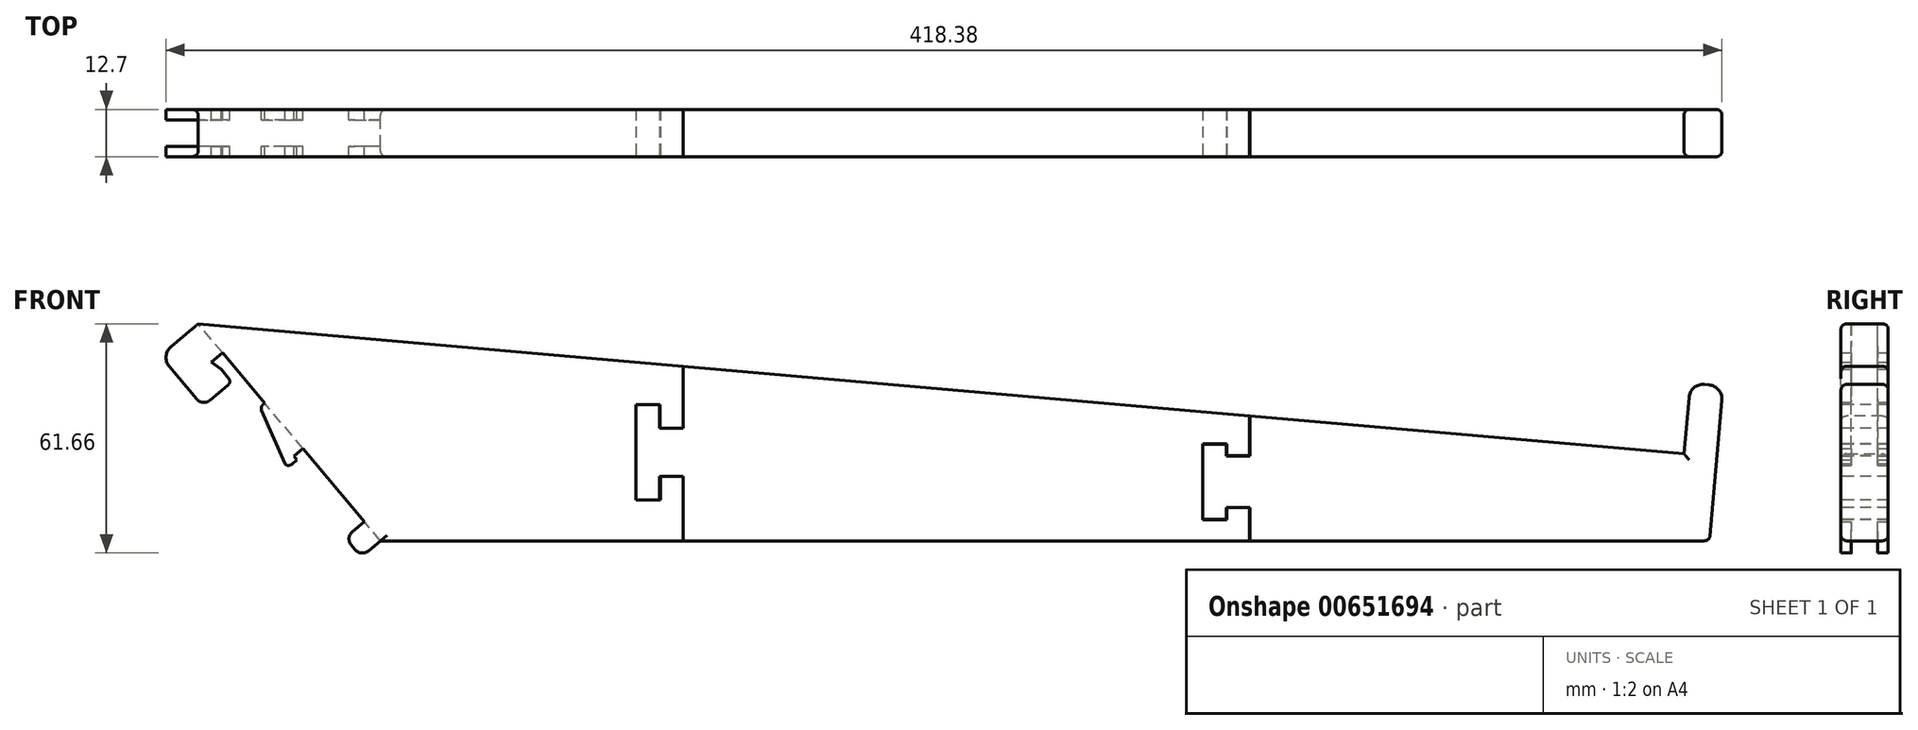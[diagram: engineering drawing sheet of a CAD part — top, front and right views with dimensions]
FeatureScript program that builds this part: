
annotation { "Feature Type Name" : "Feature", "Feature Type Description" : "" }
export const myFeature = defineFeature(function(context is Context, id is Id, definition is map)
    precondition{}
    {
        {
            var Q0;
            Q0=qCreatedBy(makeId("Front.planeOp"),FACE);
            var sketch = newSketch(context, id + "F0", { "sketchPlane" : qUnion([Q0])});
            skLineSegment(sketch, "E0.left", {"start": v(-46.53, -20.75) * mm, "end": v(-39.18, -29.5) * mm});
            skLineSegment(sketch, "E1", {"start": v(-38.77, -9.26) * mm, "end": v(360.76, -44.2) * mm});
            skLineSegment(sketch, "E2", {"start": v(360.76, -44.2) * mm, "end": v(362.09, -29.03) * mm});
            skLineSegment(sketch, "E3", {"start": v(10.22, -67.63) * mm, "end": v(367.63, -67.63) * mm});
            skPoint(sketch, "E4.start.orphan", {"position": v(-14.28, -38.44) * mm});
            skLineSegment(sketch, "E5.0", {"start": v(367.63, -67.63) * mm, "end": v(370.94, -29.8) * mm});
            skLineSegment(sketch, "E6.0", {"start": v(366.22, -25.56) * mm, "end": v(367.48, -25.67) * mm});
            skLineSegment(sketch, "E7", {"start": v(-46.06, -15.38) * mm, "end": v(-38.77, -9.26) * mm});
            skLineSegment(sketch, "E8", {"start": v(7, -70.32) * mm, "end": v(10.22, -67.63) * mm});
            skLineSegment(sketch, "E9.0", {"start": v(-12.22, -45.83) * mm, "end": v(-13.03, -44.86) * mm});
            skLineSegment(sketch, "E10.0", {"start": v(-35.6, -29.82) * mm, "end": v(-30.74, -25.73) * mm});
            skLineSegment(sketch, "E11.0", {"start": v(-30.58, -23.94) * mm, "end": v(-32.63, -21.51) * mm});
            skLineSegment(sketch, "E12.0", {"start": v(5.89, -62.47) * mm, "end": v(-10.6, -42.82) * mm});
            skLineSegment(sketch, "E13", {"start": v(-39.18, -29.5) * mm, "end": v(-46.53, -20.75) * mm});
            skLineSegment(sketch, "E14", {"start": v(-35.22, -19.55) * mm, "end": v(-32.23, -17.04) * mm});
            skArc(sketch, "E15.filletArc", {"start": v(-39.18, -29.5) * mm, "mid": v(-37.46, -30.4) * mm, "end": v(-35.6, -29.82) * mm});
            skArc(sketch, "E16.filletArc", {"start": v(-30.74, -25.73) * mm, "mid": v(-30.3, -24.87) * mm, "end": v(-30.58, -23.94) * mm});
            skLineSegment(sketch, "E17.0", {"start": v(-13.03, -44.86) * mm, "end": v(-10.6, -42.82) * mm});
            skLineSegment(sketch, "E18.0", {"start": v(6.99, -43.82) * mm, "end": v(6.99, -43.82) * mm});
            skLineSegment(sketch, "E19.0", {"start": v(-13.68, -47.06) * mm, "end": v(-12.22, -45.83) * mm});
            skLineSegment(sketch, "E20.0", {"start": v(-21.37, -30.97) * mm, "end": v(-20.89, -30.56) * mm});
            skLineSegment(sketch, "E21", {"start": v(-21.72, -32.45) * mm, "end": v(-15.47, -46.9) * mm});
            skLineSegment(sketch, "E22.trimOffspring", {"start": v(-20.89, -30.56) * mm, "end": v(-32.23, -17.04) * mm});
            skLineSegment(sketch, "E23.0", {"start": v(2.68, -65.17) * mm, "end": v(5.89, -62.47) * mm});
            skLineSegment(sketch, "E24.0", {"start": v(3.43, -70) * mm, "end": v(2.37, -68.74) * mm});
            skArc(sketch, "E25.filletArc", {"start": v(2.68, -65.17) * mm, "mid": v(1.78, -66.9) * mm, "end": v(2.37, -68.74) * mm});
            skArc(sketch, "E26.filletArc", {"start": v(3.43, -70) * mm, "mid": v(5.15, -70.9) * mm, "end": v(7, -70.32) * mm});
            skPoint(sketch, "E27.visualSharp", {"position": v(-14.65, -47.87) * mm});
            skArc(sketch, "E27.filletArc", {"start": v(-15.47, -46.9) * mm, "mid": v(-14.6, -47.35) * mm, "end": v(-13.68, -47.06) * mm});
            skPoint(sketch, "E28.visualSharp", {"position": v(-22.1, -31.58) * mm});
            skArc(sketch, "E28.filletArc", {"start": v(-21.37, -30.97) * mm, "mid": v(-21.8, -31.65) * mm, "end": v(-21.72, -32.45) * mm});
            skPoint(sketch, "E29.visualSharp", {"position": v(371.28, -26) * mm});
            skArc(sketch, "E29.filletArc", {"start": v(370.94, -29.8) * mm, "mid": v(370.07, -27.02) * mm, "end": v(367.48, -25.67) * mm});
            skPoint(sketch, "E30.visualSharp", {"position": v(362.42, -25.23) * mm});
            skArc(sketch, "E30.filletArc", {"start": v(366.22, -25.56) * mm, "mid": v(363.43, -26.44) * mm, "end": v(362.09, -29.03) * mm});
            skPoint(sketch, "E31.visualSharp", {"position": v(-48.98, -17.83) * mm});
            skArc(sketch, "E31.filletArc", {"start": v(-46.06, -15.38) * mm, "mid": v(-47.4, -17.96) * mm, "end": v(-46.53, -20.75) * mm});
            skLineSegment(sketch, "E32", {"start": v(-32.63, -21.51) * mm, "end": v(-35.22, -19.55) * mm});
            skPoint(sketch, "E33.orphan", {"position": v(-34.67, -19.08) * mm});
            skPoint(sketch, "E34.filletArc.end.orphan", {"position": v(367.94, -64.15) * mm});
            skSolve(sketch);
        }
        {
            var Q0;
            Q0=qSketchRegion(id+"F0",true);
            extrude(context, id + "F1", {"entities" : qUnion([Q0]), "depth" : 12.7 * mm, "offsetDistance" : 25.4 * mm});
        }
        {
            var Q0;
            Q0=makeQuery(id+"F1.opExtrude","SWEPT_FACE",FACE,{"disambiguationData":[OSD([sQuery(id+"F0.wireOp",EDGE,"E7")])]});
            var sketch = newSketch(context, id + "F2", { "sketchPlane" : qUnion([Q0])});
            skLineSegment(sketch, "E35.0", {"start": v(-48.98, -2.82) * mm, "end": v(-35.65, -2.82) * mm});
            skLineSegment(sketch, "E36.0", {"start": v(-35.65, -9.9) * mm, "end": v(-48.98, -9.9) * mm});
            skLineSegment(sketch, "E37", {"start": v(-35.65, -2.82) * mm, "end": v(-35.65, -9.9) * mm});
            skLineSegment(sketch, "E38", {"start": v(-48.98, -9.9) * mm, "end": v(-48.98, -2.82) * mm});
            skSolve(sketch);
        }
        {
            var Q0;
            Q0=qSketchRegion(id+"F2",true);
            extrude(context, id + "F3", {"entities" : qUnion([Q0]), "operationType" : NewBodyOperationType.REMOVE, "oppositeDirection" : true, "depth" : 93.47 * mm, "offsetDistance" : 25.4 * mm});
        }
        {
            var Q0;
            Q0=makeQuery(id+"F1.opExtrude","CAP_FACE",FACE,{"disambiguationData":[OSD([sQuery(id+"F0.wireOp",EDGE,"E1"),sQuery(id+"F0.wireOp",EDGE,"E2"),sQuery(id+"F0.wireOp",EDGE,"E3"),sQuery(id+"F0.wireOp",EDGE,"E5.0"),sQuery(id+"F0.wireOp",EDGE,"E6.0"),sQuery(id+"F0.wireOp",EDGE,"E7"),sQuery(id+"F0.wireOp",EDGE,"E8"),sQuery(id+"F0.wireOp",EDGE,"E9.0"),sQuery(id+"F0.wireOp",EDGE,"E10.0"),sQuery(id+"F0.wireOp",EDGE,"E12.0"),sQuery(id+"F0.wireOp",EDGE,"E13"),sQuery(id+"F0.wireOp",EDGE,"E14"),sQuery(id+"F0.wireOp",EDGE,"E15.filletArc"),sQuery(id+"F0.wireOp",EDGE,"E16.filletArc"),sQuery(id+"F0.wireOp",EDGE,"E17.0"),sQuery(id+"F0.wireOp",EDGE,"E19.0"),sQuery(id+"F0.wireOp",EDGE,"E20.0"),sQuery(id+"F0.wireOp",EDGE,"E11.0"),sQuery(id+"F0.wireOp",EDGE,"E21"),sQuery(id+"F0.wireOp",EDGE,"E22.trimOffspring"),sQuery(id+"F0.wireOp",EDGE,"E23.0"),sQuery(id+"F0.wireOp",EDGE,"E24.0"),sQuery(id+"F0.wireOp",EDGE,"E25.filletArc"),sQuery(id+"F0.wireOp",EDGE,"E26.filletArc"),sQuery(id+"F0.wireOp",EDGE,"E27.filletArc"),sQuery(id+"F0.wireOp",EDGE,"E28.filletArc"),sQuery(id+"F0.wireOp",EDGE,"E34.filletArc"),sQuery(id+"F0.wireOp",EDGE,"E29.filletArc"),sQuery(id+"F0.wireOp",EDGE,"E30.filletArc")])],"isStart":false});
            var sketch = newSketch(context, id + "F4", { "sketchPlane" : qUnion([Q0])});
            skLineSegment(sketch, "E39.0", {"start": v(91.68, -88.8) * mm, "end": v(91.68, -50.24) * mm});
            skLineSegment(sketch, "E40.0", {"start": v(85.33, -56.6) * mm, "end": v(85.33, -50.24) * mm});
            skLineSegment(sketch, "E41.0", {"start": v(85.33, -50.24) * mm, "end": v(91.68, -50.24) * mm});
            skLineSegment(sketch, "E42.0", {"start": v(85.33, -37.39) * mm, "end": v(91.68, -37.39) * mm});
            skLineSegment(sketch, "E43.0", {"start": v(78.98, -56.6) * mm, "end": v(78.98, -31.04) * mm});
            skLineSegment(sketch, "E44.0", {"start": v(78.98, -56.6) * mm, "end": v(85.33, -56.6) * mm});
            skLineSegment(sketch, "E45.0", {"start": v(78.98, -31.04) * mm, "end": v(85.33, -31.04) * mm});
            skLineSegment(sketch, "E46.trimOffspring", {"start": v(85.33, -37.39) * mm, "end": v(85.33, -31.04) * mm});
            skLineSegment(sketch, "E47.trimOffspring", {"start": v(91.68, -37.39) * mm, "end": v(91.68, 1.17) * mm});
            skLineSegment(sketch, "E48.0", {"start": v(91.58, -88.8) * mm, "end": v(91.58, -50.34) * mm});
            skLineSegment(sketch, "E49.0", {"start": v(85.51, -50.34) * mm, "end": v(91.58, -50.34) * mm});
            skLineSegment(sketch, "E50.0", {"start": v(85.51, -56.7) * mm, "end": v(85.51, -50.34) * mm});
            skLineSegment(sketch, "E51.0", {"start": v(78.88, -56.7) * mm, "end": v(85.51, -56.7) * mm});
            skLineSegment(sketch, "E52.0", {"start": v(78.88, -56.7) * mm, "end": v(78.88, -30.94) * mm});
            skLineSegment(sketch, "E53.0", {"start": v(78.88, -30.94) * mm, "end": v(85.43, -30.94) * mm});
            skLineSegment(sketch, "E54.0", {"start": v(85.43, -37.29) * mm, "end": v(85.43, -30.94) * mm});
            skLineSegment(sketch, "E55.0", {"start": v(85.43, -37.29) * mm, "end": v(91.58, -37.29) * mm});
            skLineSegment(sketch, "E56.0", {"start": v(91.58, -37.29) * mm, "end": v(91.58, 1.17) * mm});
            skLineSegment(sketch, "E57", {"start": v(91.68, -88.8) * mm, "end": v(91.58, -88.8) * mm});
            skLineSegment(sketch, "E58", {"start": v(91.68, 1.17) * mm, "end": v(91.58, 1.17) * mm});
            skLineSegment(sketch, "E59", {"start": v(244, -9.76) * mm, "end": v(244, -44.83) * mm});
            skLineSegment(sketch, "E60", {"start": v(237.73, -41.63) * mm, "end": v(237.73, -44.83) * mm});
            skLineSegment(sketch, "E61.0", {"start": v(231.38, -41.63) * mm, "end": v(231.38, -61.82) * mm});
            skLineSegment(sketch, "E62.0", {"start": v(237.73, -44.83) * mm, "end": v(244, -44.83) * mm});
            skLineSegment(sketch, "E63.0", {"start": v(237.73, -58.62) * mm, "end": v(244, -58.62) * mm});
            skLineSegment(sketch, "E64.0", {"start": v(231.38, -41.63) * mm, "end": v(237.73, -41.63) * mm});
            skLineSegment(sketch, "E65.0", {"start": v(231.38, -61.82) * mm, "end": v(237.73, -61.82) * mm});
            skLineSegment(sketch, "E66.trimOffspring", {"start": v(237.73, -58.62) * mm, "end": v(237.73, -61.82) * mm});
            skLineSegment(sketch, "E67.trimOffspring", {"start": v(244, -58.62) * mm, "end": v(244, -93.58) * mm});
            skLineSegment(sketch, "E68.0", {"start": v(243.9, -9.76) * mm, "end": v(243.9, -44.73) * mm});
            skLineSegment(sketch, "E68.1", {"start": v(237.83, -44.73) * mm, "end": v(243.9, -44.73) * mm});
            skLineSegment(sketch, "E68.2", {"start": v(237.83, -41.53) * mm, "end": v(237.83, -44.73) * mm});
            skLineSegment(sketch, "E68.3", {"start": v(231.28, -41.53) * mm, "end": v(237.83, -41.53) * mm});
            skLineSegment(sketch, "E68.4", {"start": v(231.28, -41.53) * mm, "end": v(231.28, -61.92) * mm});
            skLineSegment(sketch, "E68.5", {"start": v(243.9, -58.72) * mm, "end": v(243.9, -93.58) * mm});
            skLineSegment(sketch, "E68.6", {"start": v(237.83, -58.72) * mm, "end": v(243.9, -58.72) * mm});
            skLineSegment(sketch, "E68.7", {"start": v(237.83, -58.72) * mm, "end": v(237.83, -61.92) * mm});
            skLineSegment(sketch, "E68.8", {"start": v(231.28, -61.92) * mm, "end": v(237.83, -61.92) * mm});
            skLineSegment(sketch, "E69", {"start": v(244, -93.58) * mm, "end": v(243.9, -93.58) * mm});
            skLineSegment(sketch, "E70", {"start": v(244, -9.76) * mm, "end": v(243.9, -9.76) * mm});
            skLineSegment(sketch, "E71", {"start": v(-44.9, -22.7) * mm, "end": v(-27, -44.02) * mm});
            skLineSegment(sketch, "E72", {"start": v(-27, -44.02) * mm, "end": v(-46.53, -44.02) * mm});
            skLineSegment(sketch, "E73", {"start": v(-46.53, -44.02) * mm, "end": v(-47.74, -9.26) * mm});
            skLineSegment(sketch, "E74", {"start": v(-47.74, -9.26) * mm, "end": v(-38.77, -9.26) * mm});
            skSolve(sketch);
        }
        {
            var Q0;
            {var subQ0=sQuery(id+"F4.wireOp",EDGE,"E58");Q0=makeQuery(id+"F4.imprint","IMPRINT",FACE,{"disambiguationData":[TD([[makeQuery(id+"F4.imprint","IMPRINT",EDGE,{"derivedFrom":subQ0}),1.0]])]});}
            var Q1;
            Q1=makeQuery(id+"F4.imprint","IMPRINT",FACE,{"disambiguationData":[TD([[makeQuery(id+"F4.imprint","IMPRINT",EDGE,{"derivedFrom":sQuery(id+"F4.wireOp",EDGE,"E40.0")}),-1.0]])]});
            var Q2;
            {var subQ0=sQuery(id+"F4.wireOp",EDGE,"E70");Q2=makeQuery(id+"F4.imprint","IMPRINT",FACE,{"disambiguationData":[TD([[makeQuery(id+"F4.imprint","IMPRINT",EDGE,{"derivedFrom":subQ0}),1.0]])]});}
            var Q3;
            Q3=makeQuery(id+"F4.imprint","IMPRINT",FACE,{"disambiguationData":[TD([[makeQuery(id+"F4.imprint","IMPRINT",EDGE,{"derivedFrom":sQuery(id+"F4.wireOp",EDGE,"E61.0")}),-1.0]])]});
            var Q4;
            Q4=sQuery(id+"F4.wireOp",EDGE,"E56.0");
            var Q5;
            Q5=sQuery(id+"F4.wireOp",EDGE,"E48.0");
            var Q6;
            Q6=sQuery(id+"F4.wireOp",EDGE,"E39.0");
            var Q7;
            Q7=sQuery(id+"F4.wireOp",EDGE,"E47.trimOffspring");
            var Q8;
            Q8=sQuery(id+"F4.wireOp",EDGE,"E43.0");
            var Q9;
            Q9=sQuery(id+"F4.wireOp",EDGE,"E52.0");
            var Q10;
            Q10=sQuery(id+"F4.wireOp",EDGE,"E58");
            var Q11;
            Q11=sQuery(id+"F4.wireOp",EDGE,"E57");
            var Q12;
            Q12=sQuery(id+"F4.wireOp",EDGE,"E45.0");
            var Q13;
            Q13=sQuery(id+"F4.wireOp",EDGE,"E54.0");
            var Q14;
            Q14=sQuery(id+"F4.wireOp",EDGE,"E53.0");
            var Q15;
            Q15=sQuery(id+"F4.wireOp",EDGE,"E49.0");
            var Q16;
            Q16=sQuery(id+"F4.wireOp",EDGE,"E46.trimOffspring");
            var Q17;
            Q17=sQuery(id+"F4.wireOp",EDGE,"E44.0");
            var Q18;
            Q18=sQuery(id+"F4.wireOp",EDGE,"E42.0");
            var Q19;
            Q19=sQuery(id+"F4.wireOp",EDGE,"E55.0");
            var Q20;
            Q20=sQuery(id+"F4.wireOp",EDGE,"E50.0");
            var Q21;
            Q21=sQuery(id+"F4.wireOp",EDGE,"E51.0");
            var Q22;
            Q22=sQuery(id+"F4.wireOp",EDGE,"E40.0");
            var Q23;
            Q23=sQuery(id+"F4.wireOp",EDGE,"E41.0");
            extrude(context, id + "F5", {"entities" : qUnion([Q0, Q1, Q2, Q3]), "operationType" : NewBodyOperationType.REMOVE, "surfaceEntities" : qUnion([Q4, Q5, Q6, Q7, Q8, Q9, Q10, Q11, Q12, Q13, Q14, Q15, Q16, Q17, Q18, Q19, Q20, Q21, Q22, Q23]), "oppositeDirection" : true, "depth" : 25.4 * mm, "offsetDistance" : 25.4 * mm});
        }
        {
            var Q0;
            {var subQ0=sQuery(id+"F0.wireOp",EDGE,"E1");var subQ1=sQuery(id+"F0.wireOp",EDGE,"E7");Q0=makeQuery(id+"F5.boolean.opBoolean","SPLIT",EDGE,{"disambiguationData":[TD([makeQuery(id+"F1.opExtrude","SWEPT_FACE",FACE,{"disambiguationData":[OSD([subQ1])]})])],"derivedFrom":makeQuery(id+"F1.opExtrude","CAP_EDGE",EDGE,{"disambiguationData":[OSD([subQ0])],"isStart":true})});}
            var Q1;
            {var subQ0=sQuery(id+"F0.wireOp",EDGE,"E1");Q1=makeQuery(id+"F5.boolean.opBoolean","SPLIT",EDGE,{"disambiguationData":[TD([makeQuery(id+"F5.opExtrude","SWEPT_FACE",FACE,{"disambiguationData":[OSD([sQuery(id+"F4.wireOp",EDGE,"E47.trimOffspring")])]})])],"derivedFrom":makeQuery(id+"F1.opExtrude","CAP_EDGE",EDGE,{"disambiguationData":[OSD([subQ0])],"isStart":true})});}
            var Q2;
            {var subQ0=sQuery(id+"F0.wireOp",EDGE,"E1");var subQ1=sQuery(id+"F0.wireOp",EDGE,"E2");Q2=makeQuery(id+"F5.boolean.opBoolean","SPLIT",EDGE,{"disambiguationData":[TD([makeQuery(id+"F1.opExtrude","SWEPT_FACE",FACE,{"disambiguationData":[OSD([subQ1])]})])],"derivedFrom":makeQuery(id+"F1.opExtrude","CAP_EDGE",EDGE,{"disambiguationData":[OSD([subQ0])],"isStart":true})});}
            var Q3;
            Q3=makeQuery(id+"F1.opExtrude","CAP_EDGE",EDGE,{"disambiguationData":[OSD([sQuery(id+"F0.wireOp",EDGE,"E2")])],"isStart":true});
            var Q4;
            {var subQ0=sQuery(id+"F0.wireOp",EDGE,"E3");Q4=makeQuery(id+"F5.boolean.opBoolean","SPLIT",EDGE,{"disambiguationData":[TD([makeQuery(id+"F5.opExtrude","SWEPT_FACE",FACE,{"disambiguationData":[OSD([sQuery(id+"F4.wireOp",EDGE,"E39.0")])]})])],"derivedFrom":makeQuery(id+"F1.opExtrude","CAP_EDGE",EDGE,{"disambiguationData":[OSD([subQ0])],"isStart":true})});}
            var Q5;
            {var subQ0=sQuery(id+"F0.wireOp",EDGE,"E8");var subQ1=sQuery(id+"F0.wireOp",EDGE,"E3");Q5=makeQuery(id+"F5.boolean.opBoolean","SPLIT",EDGE,{"disambiguationData":[TD([makeQuery(id+"F1.opExtrude","SWEPT_FACE",FACE,{"disambiguationData":[OSD([subQ0])]})])],"derivedFrom":makeQuery(id+"F1.opExtrude","CAP_EDGE",EDGE,{"disambiguationData":[OSD([subQ1])],"isStart":true})});}
            fillet(context, id + "F6", {"entities" : qUnion([Q0, Q1, Q2, Q3, Q4, Q5]), "radius" : 1.52 * mm, "tangentPropagation" : true, "allowEdgeOverflow" : false});
        }
        {
            var Q0;
            {var subQ0=sQuery(id+"F0.wireOp",EDGE,"E1");var subQ1=sQuery(id+"F0.wireOp",EDGE,"E7");Q0=makeQuery(id+"F5.boolean.opBoolean","SPLIT",EDGE,{"disambiguationData":[TD([makeQuery(id+"F1.opExtrude","SWEPT_FACE",FACE,{"disambiguationData":[OSD([subQ1])]})])],"derivedFrom":makeQuery(id+"F1.opExtrude","CAP_EDGE",EDGE,{"disambiguationData":[OSD([subQ0])],"isStart":false})});}
            var Q1;
            {var subQ0=sQuery(id+"F0.wireOp",EDGE,"E1");Q1=makeQuery(id+"F5.boolean.opBoolean","SPLIT",EDGE,{"disambiguationData":[TD([makeQuery(id+"F5.opExtrude","SWEPT_FACE",FACE,{"disambiguationData":[OSD([sQuery(id+"F4.wireOp",EDGE,"E47.trimOffspring")])]})])],"derivedFrom":makeQuery(id+"F1.opExtrude","CAP_EDGE",EDGE,{"disambiguationData":[OSD([subQ0])],"isStart":false})});}
            var Q2;
            {var subQ0=sQuery(id+"F0.wireOp",EDGE,"E1");var subQ1=sQuery(id+"F0.wireOp",EDGE,"E2");Q2=makeQuery(id+"F5.boolean.opBoolean","SPLIT",EDGE,{"disambiguationData":[TD([makeQuery(id+"F1.opExtrude","SWEPT_FACE",FACE,{"disambiguationData":[OSD([subQ1])]})])],"derivedFrom":makeQuery(id+"F1.opExtrude","CAP_EDGE",EDGE,{"disambiguationData":[OSD([subQ0])],"isStart":false})});}
            var Q3;
            Q3=makeQuery(id+"F1.opExtrude","CAP_EDGE",EDGE,{"disambiguationData":[OSD([sQuery(id+"F0.wireOp",EDGE,"E2")])],"isStart":false});
            var Q4;
            {var subQ0=sQuery(id+"F0.wireOp",EDGE,"E3");Q4=makeQuery(id+"F5.boolean.opBoolean","SPLIT",EDGE,{"disambiguationData":[TD([makeQuery(id+"F5.opExtrude","SWEPT_FACE",FACE,{"disambiguationData":[OSD([sQuery(id+"F4.wireOp",EDGE,"E39.0")])]})])],"derivedFrom":makeQuery(id+"F1.opExtrude","CAP_EDGE",EDGE,{"disambiguationData":[OSD([subQ0])],"isStart":false})});}
            var Q5;
            {var subQ0=sQuery(id+"F0.wireOp",EDGE,"E8");var subQ1=sQuery(id+"F0.wireOp",EDGE,"E3");Q5=makeQuery(id+"F5.boolean.opBoolean","SPLIT",EDGE,{"disambiguationData":[TD([makeQuery(id+"F1.opExtrude","SWEPT_FACE",FACE,{"disambiguationData":[OSD([subQ0])]})])],"derivedFrom":makeQuery(id+"F1.opExtrude","CAP_EDGE",EDGE,{"disambiguationData":[OSD([subQ1])],"isStart":false})});}
            fillet(context, id + "F7", {"entities" : qUnion([Q0, Q1, Q2, Q3, Q4, Q5]), "radius" : 1.52 * mm, "tangentPropagation" : true, "allowEdgeOverflow" : false});
        }
        {
            var Q0;
            Q0=qCreatedBy(makeId("Right.planeOp"),FACE);
            var sketch = newSketch(context, id + "F8", { "sketchPlane" : qUnion([Q0])});
            skLineSegment(sketch, "E75.top", {"start": v(-9.53, 0) * mm, "end": v(-3.18, 0) * mm});
            skLineSegment(sketch, "E76.0", {"start": v(-9.52, -64.44) * mm, "end": v(-9.53, 0) * mm});
            skLineSegment(sketch, "E77.0", {"start": v(-3.17, -64.44) * mm, "end": v(-3.18, 0) * mm});
            skLineSegment(sketch, "E78.0", {"start": v(-3.17, -64.44) * mm, "end": v(-9.52, -64.44) * mm});
            skSolve(sketch);
        }
        {
            var Q0;
            Q0=makeQuery(id+"F1.opExtrude","SWEPT_FACE",FACE,{"disambiguationData":[OSD([sQuery(id+"F0.wireOp",EDGE,"E8")])]});
            var sketch = newSketch(context, id + "F9", { "sketchPlane" : qUnion([Q0])});
            skLineSegment(sketch, "E79.0", {"start": v(-35.65, 9.53) * mm, "end": v(-47.4, 9.53) * mm});
            skLineSegment(sketch, "E80.0", {"start": v(-35.65, 3.18) * mm, "end": v(-47.4, 3.17) * mm});
            skLineSegment(sketch, "E81", {"start": v(-47.4, 9.53) * mm, "end": v(-47.4, 3.17) * mm});
            skPoint(sketch, "E82.top.end.orphan", {"position": v(-47.4, 0) * mm});
            skLineSegment(sketch, "E83", {"start": v(-35.65, 3.18) * mm, "end": v(-35.65, 9.53) * mm});
            skSolve(sketch);
        }
        {
            var Q0;
            {var subQ0=sQuery(id+"F0.wireOp",EDGE,"E5.0");var subQ1=sQuery(id+"F0.wireOp",EDGE,"E3");Q0=makeQuery(id+"F5.boolean.opBoolean","SPLIT",EDGE,{"disambiguationData":[TD([makeQuery(id+"F1.opExtrude","SWEPT_FACE",FACE,{"disambiguationData":[OSD([subQ0])]})])],"derivedFrom":makeQuery(id+"F1.opExtrude","CAP_EDGE",EDGE,{"disambiguationData":[OSD([subQ1])],"isStart":false})});}
            fillet(context, id + "F10", {"entities" : qUnion([Q0]), "radius" : 1.52 * mm, "tangentPropagation" : true, "allowEdgeOverflow" : false});
        }
    });
